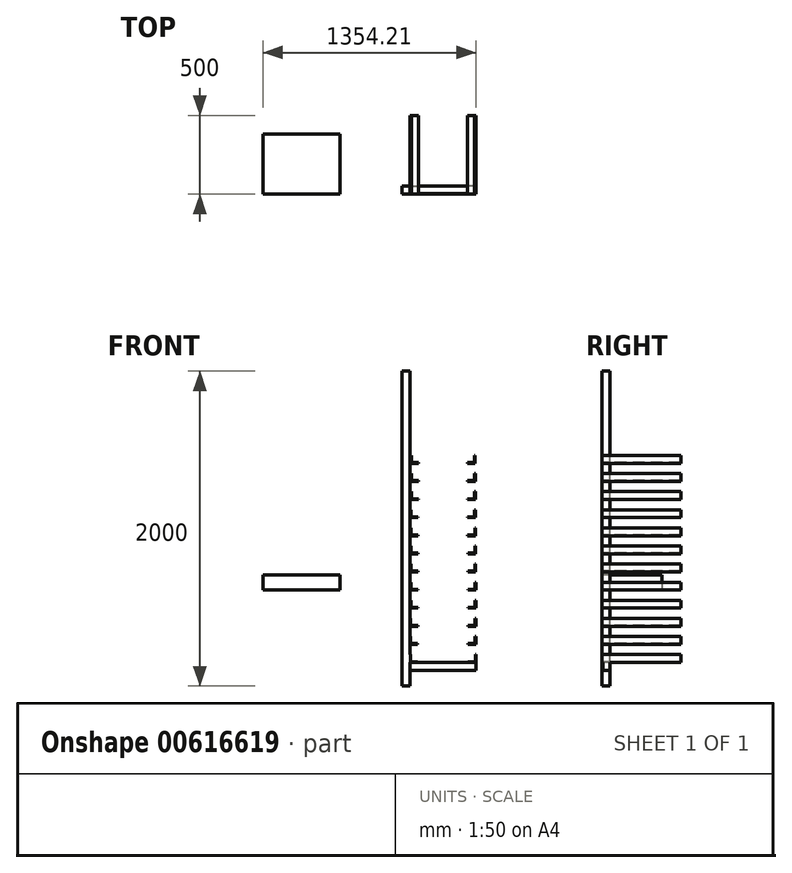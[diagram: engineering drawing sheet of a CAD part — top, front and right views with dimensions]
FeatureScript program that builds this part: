
annotation { "Feature Type Name" : "Feature", "Feature Type Description" : "" }
export const myFeature = defineFeature(function(context is Context, id is Id, definition is map)
    precondition{}
    {
        {
            var Q0;
            Q0=qCreatedBy(makeId("Front.planeOp"),FACE);
            var sketch = newSketch(context, id + "F0", { "sketchPlane" : qUnion([Q0])});
            skLineSegment(sketch, "E0.bottom", {"start": v(-1078.95, 84.72) * mm, "end": v(-1028.95, 84.72) * mm});
            skLineSegment(sketch, "E0.top", {"start": v(-1078.95, 2084.72) * mm, "end": v(-1028.95, 2084.72) * mm});
            skLineSegment(sketch, "E0.left", {"start": v(-1078.95, 84.72) * mm, "end": v(-1078.95, 2084.72) * mm});
            skLineSegment(sketch, "E0.right", {"start": v(-1028.95, 84.72) * mm, "end": v(-1028.95, 2084.72) * mm});
            skLineSegment(sketch, "E1.bottom", {"start": v(-1028.95, 234.72) * mm, "end": v(-607.88, 234.72) * mm});
            skLineSegment(sketch, "E1.top", {"start": v(-1028.95, 184.72) * mm, "end": v(-607.88, 184.72) * mm});
            skLineSegment(sketch, "E1.left", {"start": v(-1028.95, 234.72) * mm, "end": v(-1028.95, 184.72) * mm});
            skLineSegment(sketch, "E1.right", {"start": v(-607.88, 234.72) * mm, "end": v(-607.88, 184.72) * mm});
            skPoint(sketch, "E2", {"position": v(-1028.95, 209.72) * mm});
            skLineSegment(sketch, "E3", {"start": v(-1023.95, 284.72) * mm, "end": v(-1023.95, 239.72) * mm});
            skLineSegment(sketch, "E4", {"start": v(-1023.95, 239.72) * mm, "end": v(-978.95, 239.72) * mm});
            skLineSegment(sketch, "E5", {"start": v(-1023.95, 284.72) * mm, "end": v(-1028.95, 284.72) * mm});
            skLineSegment(sketch, "E6", {"start": v(-1028.95, 284.72) * mm, "end": v(-1028.95, 234.72) * mm});
            skLineSegment(sketch, "E7", {"start": v(-1028.95, 234.72) * mm, "end": v(-978.95, 234.72) * mm});
            skLineSegment(sketch, "E8", {"start": v(-978.95, 234.72) * mm, "end": v(-978.95, 239.72) * mm});
            skLineSegment(sketch, "E9.0.1.0", {"start": v(-1028.46, 399.72) * mm, "end": v(-1028.46, 349.72) * mm});
            skLineSegment(sketch, "E9.0.1.1", {"start": v(-1023.46, 354.72) * mm, "end": v(-978.46, 354.72) * mm});
            skLineSegment(sketch, "E9.0.1.2", {"start": v(-1028.46, 349.72) * mm, "end": v(-978.46, 349.72) * mm});
            skLineSegment(sketch, "E9.0.1.3", {"start": v(-1023.46, 399.72) * mm, "end": v(-1023.46, 354.72) * mm});
            skLineSegment(sketch, "E9.0.1.4", {"start": v(-978.46, 349.72) * mm, "end": v(-978.46, 354.72) * mm});
            skLineSegment(sketch, "E9.0.1.5", {"start": v(-1023.46, 399.72) * mm, "end": v(-1028.46, 399.72) * mm});
            skLineSegment(sketch, "E9.0.2.0", {"start": v(-1027.98, 514.72) * mm, "end": v(-1027.98, 464.72) * mm});
            skLineSegment(sketch, "E9.0.2.1", {"start": v(-1022.98, 469.72) * mm, "end": v(-977.98, 469.72) * mm});
            skLineSegment(sketch, "E9.0.2.2", {"start": v(-1027.98, 464.72) * mm, "end": v(-977.98, 464.72) * mm});
            skLineSegment(sketch, "E9.0.2.3", {"start": v(-1022.98, 514.72) * mm, "end": v(-1022.98, 469.72) * mm});
            skLineSegment(sketch, "E9.0.2.4", {"start": v(-977.98, 464.72) * mm, "end": v(-977.98, 469.72) * mm});
            skLineSegment(sketch, "E9.0.2.5", {"start": v(-1022.98, 514.72) * mm, "end": v(-1027.98, 514.72) * mm});
            skLineSegment(sketch, "E9.0.3.0", {"start": v(-1027.5, 629.72) * mm, "end": v(-1027.5, 579.72) * mm});
            skLineSegment(sketch, "E9.0.3.1", {"start": v(-1022.5, 584.72) * mm, "end": v(-977.5, 584.72) * mm});
            skLineSegment(sketch, "E9.0.3.2", {"start": v(-1027.5, 579.72) * mm, "end": v(-977.5, 579.72) * mm});
            skLineSegment(sketch, "E9.0.3.3", {"start": v(-1022.5, 629.72) * mm, "end": v(-1022.5, 584.72) * mm});
            skLineSegment(sketch, "E9.0.3.4", {"start": v(-977.5, 579.72) * mm, "end": v(-977.5, 584.72) * mm});
            skLineSegment(sketch, "E9.0.3.5", {"start": v(-1022.5, 629.72) * mm, "end": v(-1027.5, 629.72) * mm});
            skLineSegment(sketch, "E9.0.4.0", {"start": v(-1027.01, 744.72) * mm, "end": v(-1027.01, 694.72) * mm});
            skLineSegment(sketch, "E9.0.4.1", {"start": v(-1022.01, 699.72) * mm, "end": v(-977.01, 699.72) * mm});
            skLineSegment(sketch, "E9.0.4.2", {"start": v(-1027.01, 694.72) * mm, "end": v(-977.01, 694.72) * mm});
            skLineSegment(sketch, "E9.0.4.3", {"start": v(-1022.01, 744.72) * mm, "end": v(-1022.01, 699.72) * mm});
            skLineSegment(sketch, "E9.0.4.4", {"start": v(-977.01, 694.72) * mm, "end": v(-977.01, 699.72) * mm});
            skLineSegment(sketch, "E9.0.4.5", {"start": v(-1022.01, 744.72) * mm, "end": v(-1027.01, 744.72) * mm});
            skLineSegment(sketch, "E9.0.5.0", {"start": v(-1026.53, 859.72) * mm, "end": v(-1026.53, 809.72) * mm});
            skLineSegment(sketch, "E9.0.5.1", {"start": v(-1021.53, 814.72) * mm, "end": v(-976.53, 814.72) * mm});
            skLineSegment(sketch, "E9.0.5.2", {"start": v(-1026.53, 809.72) * mm, "end": v(-976.53, 809.72) * mm});
            skLineSegment(sketch, "E9.0.5.3", {"start": v(-1021.53, 859.72) * mm, "end": v(-1021.53, 814.72) * mm});
            skLineSegment(sketch, "E9.0.5.4", {"start": v(-976.53, 809.72) * mm, "end": v(-976.53, 814.72) * mm});
            skLineSegment(sketch, "E9.0.5.5", {"start": v(-1021.53, 859.72) * mm, "end": v(-1026.53, 859.72) * mm});
            skLineSegment(sketch, "E9.0.6.0", {"start": v(-1026.04, 974.71) * mm, "end": v(-1026.04, 924.71) * mm});
            skLineSegment(sketch, "E9.0.6.1", {"start": v(-1021.04, 929.71) * mm, "end": v(-976.04, 929.71) * mm});
            skLineSegment(sketch, "E9.0.6.2", {"start": v(-1026.04, 924.71) * mm, "end": v(-976.04, 924.71) * mm});
            skLineSegment(sketch, "E9.0.6.3", {"start": v(-1021.04, 974.71) * mm, "end": v(-1021.04, 929.71) * mm});
            skLineSegment(sketch, "E9.0.6.4", {"start": v(-976.04, 924.71) * mm, "end": v(-976.04, 929.71) * mm});
            skLineSegment(sketch, "E9.0.6.5", {"start": v(-1021.04, 974.71) * mm, "end": v(-1026.04, 974.71) * mm});
            skLineSegment(sketch, "E9.0.7.0", {"start": v(-1025.56, 1089.71) * mm, "end": v(-1025.56, 1039.71) * mm});
            skLineSegment(sketch, "E9.0.7.1", {"start": v(-1020.56, 1044.71) * mm, "end": v(-975.56, 1044.71) * mm});
            skLineSegment(sketch, "E9.0.7.2", {"start": v(-1025.56, 1039.71) * mm, "end": v(-975.56, 1039.71) * mm});
            skLineSegment(sketch, "E9.0.7.3", {"start": v(-1020.56, 1089.71) * mm, "end": v(-1020.56, 1044.71) * mm});
            skLineSegment(sketch, "E9.0.7.4", {"start": v(-975.56, 1039.71) * mm, "end": v(-975.56, 1044.71) * mm});
            skLineSegment(sketch, "E9.0.7.5", {"start": v(-1020.56, 1089.71) * mm, "end": v(-1025.56, 1089.71) * mm});
            skLineSegment(sketch, "E9.0.8.0", {"start": v(-1025.07, 1204.71) * mm, "end": v(-1025.07, 1154.71) * mm});
            skLineSegment(sketch, "E9.0.8.1", {"start": v(-1020.07, 1159.71) * mm, "end": v(-975.07, 1159.71) * mm});
            skLineSegment(sketch, "E9.0.8.2", {"start": v(-1025.07, 1154.71) * mm, "end": v(-975.07, 1154.71) * mm});
            skLineSegment(sketch, "E9.0.8.3", {"start": v(-1020.07, 1204.71) * mm, "end": v(-1020.07, 1159.71) * mm});
            skLineSegment(sketch, "E9.0.8.4", {"start": v(-975.07, 1154.71) * mm, "end": v(-975.07, 1159.71) * mm});
            skLineSegment(sketch, "E9.0.8.5", {"start": v(-1020.07, 1204.71) * mm, "end": v(-1025.07, 1204.71) * mm});
            skLineSegment(sketch, "E9.0.9.0", {"start": v(-1024.59, 1319.71) * mm, "end": v(-1024.59, 1269.71) * mm});
            skLineSegment(sketch, "E9.0.9.1", {"start": v(-1019.59, 1274.71) * mm, "end": v(-974.59, 1274.71) * mm});
            skLineSegment(sketch, "E9.0.9.2", {"start": v(-1024.59, 1269.71) * mm, "end": v(-974.59, 1269.71) * mm});
            skLineSegment(sketch, "E9.0.9.3", {"start": v(-1019.59, 1319.71) * mm, "end": v(-1019.59, 1274.71) * mm});
            skLineSegment(sketch, "E9.0.9.4", {"start": v(-974.59, 1269.71) * mm, "end": v(-974.59, 1274.71) * mm});
            skLineSegment(sketch, "E9.0.9.5", {"start": v(-1019.59, 1319.71) * mm, "end": v(-1024.59, 1319.71) * mm});
            skLineSegment(sketch, "E9.0.10.0", {"start": v(-1024.1, 1434.71) * mm, "end": v(-1024.1, 1384.71) * mm});
            skLineSegment(sketch, "E9.0.10.1", {"start": v(-1019.1, 1389.71) * mm, "end": v(-974.1, 1389.71) * mm});
            skLineSegment(sketch, "E9.0.10.2", {"start": v(-1024.1, 1384.71) * mm, "end": v(-974.1, 1384.71) * mm});
            skLineSegment(sketch, "E9.0.10.3", {"start": v(-1019.1, 1434.71) * mm, "end": v(-1019.1, 1389.71) * mm});
            skLineSegment(sketch, "E9.0.10.4", {"start": v(-974.1, 1384.71) * mm, "end": v(-974.1, 1389.71) * mm});
            skLineSegment(sketch, "E9.0.10.5", {"start": v(-1019.1, 1434.71) * mm, "end": v(-1024.1, 1434.71) * mm});
            skLineSegment(sketch, "E9.0.11.0", {"start": v(-1023.62, 1549.7) * mm, "end": v(-1023.62, 1499.7) * mm});
            skLineSegment(sketch, "E9.0.11.1", {"start": v(-1018.62, 1504.7) * mm, "end": v(-973.62, 1504.7) * mm});
            skLineSegment(sketch, "E9.0.11.2", {"start": v(-1023.62, 1499.7) * mm, "end": v(-973.62, 1499.7) * mm});
            skLineSegment(sketch, "E9.0.11.3", {"start": v(-1018.62, 1549.7) * mm, "end": v(-1018.62, 1504.7) * mm});
            skLineSegment(sketch, "E9.0.11.4", {"start": v(-973.62, 1499.7) * mm, "end": v(-973.62, 1504.7) * mm});
            skLineSegment(sketch, "E9.0.11.5", {"start": v(-1018.62, 1549.7) * mm, "end": v(-1023.62, 1549.7) * mm});
            skLineSegment(sketch, "E9.direction1", {"start": v(-1028.95, 234.72) * mm, "end": v(-950, 234.72) * mm, "construction": true});
            skLineSegment(sketch, "E9.direction2", {"start": v(-1028.95, 234.72) * mm, "end": v(-1028.46, 349.72) * mm, "construction": true});
            skLineSegment(sketch, "E10", {"start": v(-818.42, 234.72) * mm, "end": v(-818.42, 1014.16) * mm, "construction": true});
            skLineSegment(sketch, "E11.MirrorCS", {"start": v(-660.8, 924.71) * mm, "end": v(-660.8, 929.71) * mm});
            skLineSegment(sketch, "E12.MirrorCS", {"start": v(-616.27, 1089.71) * mm, "end": v(-611.27, 1089.71) * mm});
            skLineSegment(sketch, "E13.MirrorCS", {"start": v(-661.27, 1039.71) * mm, "end": v(-661.27, 1044.71) * mm});
            skLineSegment(sketch, "E14.MirrorCS", {"start": v(-616.27, 1044.71) * mm, "end": v(-661.27, 1044.71) * mm});
            skLineSegment(sketch, "E15.MirrorCS", {"start": v(-615.8, 929.71) * mm, "end": v(-660.8, 929.71) * mm});
            skLineSegment(sketch, "E16.MirrorCS", {"start": v(-617.24, 1319.71) * mm, "end": v(-612.24, 1319.71) * mm});
            skLineSegment(sketch, "E17.MirrorCS", {"start": v(-611.27, 1089.71) * mm, "end": v(-611.27, 1039.71) * mm});
            skLineSegment(sketch, "E18.MirrorCS", {"start": v(-618.21, 1504.7) * mm, "end": v(-663.21, 1504.7) * mm});
            skLineSegment(sketch, "E19.MirrorCS", {"start": v(-615.8, 974.71) * mm, "end": v(-610.8, 974.71) * mm});
            skLineSegment(sketch, "E20.MirrorCS", {"start": v(-617.24, 1319.71) * mm, "end": v(-617.24, 1274.71) * mm});
            skLineSegment(sketch, "E21.MirrorCS", {"start": v(-662.73, 1384.71) * mm, "end": v(-662.73, 1389.71) * mm});
            skLineSegment(sketch, "E22.MirrorCS", {"start": v(-611.76, 1204.71) * mm, "end": v(-611.76, 1154.71) * mm});
            skLineSegment(sketch, "E23.MirrorCS", {"start": v(-616.76, 1159.71) * mm, "end": v(-661.76, 1159.71) * mm});
            skLineSegment(sketch, "E24.MirrorCS", {"start": v(-617.73, 1434.71) * mm, "end": v(-617.73, 1389.71) * mm});
            skLineSegment(sketch, "E25.MirrorCS", {"start": v(-615.8, 974.71) * mm, "end": v(-615.8, 929.71) * mm});
            skLineSegment(sketch, "E26.MirrorCS", {"start": v(-617.24, 1274.71) * mm, "end": v(-662.24, 1274.71) * mm});
            skLineSegment(sketch, "E27.MirrorCS", {"start": v(-618.21, 1549.7) * mm, "end": v(-613.21, 1549.7) * mm});
            skLineSegment(sketch, "E28.MirrorCS", {"start": v(-612.73, 1384.71) * mm, "end": v(-662.73, 1384.71) * mm});
            skLineSegment(sketch, "E29.MirrorCS", {"start": v(-611.27, 1039.71) * mm, "end": v(-661.27, 1039.71) * mm});
            skLineSegment(sketch, "E30.MirrorCS", {"start": v(-612.73, 1434.71) * mm, "end": v(-612.73, 1384.71) * mm});
            skLineSegment(sketch, "E31.MirrorCS", {"start": v(-661.76, 1154.71) * mm, "end": v(-661.76, 1159.71) * mm});
            skLineSegment(sketch, "E32.MirrorCS", {"start": v(-616.27, 1089.71) * mm, "end": v(-616.27, 1044.71) * mm});
            skLineSegment(sketch, "E33.MirrorCS", {"start": v(-610.8, 974.71) * mm, "end": v(-610.8, 924.71) * mm});
            skLineSegment(sketch, "E34.MirrorCS", {"start": v(-616.76, 1204.71) * mm, "end": v(-611.76, 1204.71) * mm});
            skLineSegment(sketch, "E35.MirrorCS", {"start": v(-663.21, 1499.7) * mm, "end": v(-663.21, 1504.7) * mm});
            skLineSegment(sketch, "E36.MirrorCS", {"start": v(-618.21, 1549.7) * mm, "end": v(-618.21, 1504.7) * mm});
            skLineSegment(sketch, "E37.MirrorCS", {"start": v(-613.21, 1499.7) * mm, "end": v(-663.21, 1499.7) * mm});
            skLineSegment(sketch, "E38.MirrorCS", {"start": v(-617.73, 1389.71) * mm, "end": v(-662.73, 1389.71) * mm});
            skLineSegment(sketch, "E39.MirrorCS", {"start": v(-612.88, 284.72) * mm, "end": v(-607.88, 284.72) * mm});
            skLineSegment(sketch, "E40.MirrorCS", {"start": v(-662.24, 1269.71) * mm, "end": v(-662.24, 1274.71) * mm});
            skLineSegment(sketch, "E41.MirrorCS", {"start": v(-616.76, 1204.71) * mm, "end": v(-616.76, 1159.71) * mm});
            skLineSegment(sketch, "E42.MirrorCS", {"start": v(-658.37, 349.72) * mm, "end": v(-658.37, 354.72) * mm});
            skLineSegment(sketch, "E43.MirrorCS", {"start": v(-659.34, 579.72) * mm, "end": v(-659.34, 584.72) * mm});
            skLineSegment(sketch, "E44.MirrorCS", {"start": v(-660.3, 809.72) * mm, "end": v(-660.3, 814.72) * mm});
            skLineSegment(sketch, "E45.MirrorCS", {"start": v(-611.76, 1154.71) * mm, "end": v(-661.76, 1154.71) * mm});
            skLineSegment(sketch, "E46.MirrorCS", {"start": v(-613.21, 1549.7) * mm, "end": v(-613.21, 1499.7) * mm});
            skLineSegment(sketch, "E47.MirrorCS", {"start": v(-612.24, 1269.71) * mm, "end": v(-662.24, 1269.71) * mm});
            skLineSegment(sketch, "E48.MirrorCS", {"start": v(-617.73, 1434.71) * mm, "end": v(-612.73, 1434.71) * mm});
            skLineSegment(sketch, "E49.MirrorCS", {"start": v(-608.37, 349.72) * mm, "end": v(-658.37, 349.72) * mm});
            skLineSegment(sketch, "E50.MirrorCS", {"start": v(-615.3, 814.72) * mm, "end": v(-660.3, 814.72) * mm});
            skLineSegment(sketch, "E51.MirrorCS", {"start": v(-613.37, 354.72) * mm, "end": v(-658.37, 354.72) * mm});
            skLineSegment(sketch, "E52.MirrorCS", {"start": v(-612.24, 1319.71) * mm, "end": v(-612.24, 1269.71) * mm});
            skLineSegment(sketch, "E53.MirrorCS", {"start": v(-610.8, 924.71) * mm, "end": v(-660.8, 924.71) * mm});
            skLineSegment(sketch, "E54.MirrorCS", {"start": v(-607.88, 234.72) * mm, "end": v(-657.88, 234.72) * mm});
            skLineSegment(sketch, "E55.MirrorCS", {"start": v(-614.82, 744.72) * mm, "end": v(-614.82, 699.72) * mm});
            skLineSegment(sketch, "E56.MirrorCS", {"start": v(-609.34, 579.72) * mm, "end": v(-659.34, 579.72) * mm});
            skLineSegment(sketch, "E57.MirrorCS", {"start": v(-607.88, 284.72) * mm, "end": v(-607.88, 234.72) * mm});
            skLineSegment(sketch, "E58.MirrorCS", {"start": v(-612.88, 239.72) * mm, "end": v(-657.88, 239.72) * mm});
            skLineSegment(sketch, "E59.MirrorCS", {"start": v(-609.82, 694.72) * mm, "end": v(-659.82, 694.72) * mm});
            skLineSegment(sketch, "E60.MirrorCS", {"start": v(-614.34, 584.72) * mm, "end": v(-659.34, 584.72) * mm});
            skLineSegment(sketch, "E61.MirrorCS", {"start": v(-614.82, 699.72) * mm, "end": v(-659.82, 699.72) * mm});
            skLineSegment(sketch, "E62.MirrorCS", {"start": v(-658.85, 464.72) * mm, "end": v(-658.85, 469.72) * mm});
            skLineSegment(sketch, "E63.MirrorCS", {"start": v(-610.3, 809.72) * mm, "end": v(-660.3, 809.72) * mm});
            skLineSegment(sketch, "E64.MirrorCS", {"start": v(-609.82, 744.72) * mm, "end": v(-609.82, 694.72) * mm});
            skLineSegment(sketch, "E65.MirrorCS", {"start": v(-613.85, 514.72) * mm, "end": v(-608.85, 514.72) * mm});
            skLineSegment(sketch, "E66.MirrorCS", {"start": v(-614.82, 744.72) * mm, "end": v(-609.82, 744.72) * mm});
            skLineSegment(sketch, "E67.MirrorCS", {"start": v(-614.34, 629.72) * mm, "end": v(-614.34, 584.72) * mm});
            skLineSegment(sketch, "E68.MirrorCS", {"start": v(-608.85, 514.72) * mm, "end": v(-608.85, 464.72) * mm});
            skLineSegment(sketch, "E69.MirrorCS", {"start": v(-659.82, 694.72) * mm, "end": v(-659.82, 699.72) * mm});
            skLineSegment(sketch, "E70.MirrorCS", {"start": v(-613.85, 469.72) * mm, "end": v(-658.85, 469.72) * mm});
            skLineSegment(sketch, "E71.MirrorCS", {"start": v(-608.37, 399.72) * mm, "end": v(-608.37, 349.72) * mm});
            skLineSegment(sketch, "E72.MirrorCS", {"start": v(-657.88, 234.72) * mm, "end": v(-657.88, 239.72) * mm});
            skLineSegment(sketch, "E73.MirrorCS", {"start": v(-613.37, 399.72) * mm, "end": v(-608.37, 399.72) * mm});
            skLineSegment(sketch, "E74.MirrorCS", {"start": v(-612.88, 284.72) * mm, "end": v(-612.88, 239.72) * mm});
            skLineSegment(sketch, "E75.MirrorCS", {"start": v(-615.3, 859.72) * mm, "end": v(-610.3, 859.72) * mm});
            skLineSegment(sketch, "E76.MirrorCS", {"start": v(-609.34, 629.72) * mm, "end": v(-609.34, 579.72) * mm});
            skLineSegment(sketch, "E77.MirrorCS", {"start": v(-607.88, 234.72) * mm, "end": v(-686.82, 234.72) * mm, "construction": true});
            skLineSegment(sketch, "E78.MirrorCS", {"start": v(-607.88, 234.72) * mm, "end": v(-608.37, 349.72) * mm, "construction": true});
            skLineSegment(sketch, "E79.MirrorCS", {"start": v(-613.37, 399.72) * mm, "end": v(-613.37, 354.72) * mm});
            skLineSegment(sketch, "E80.MirrorCS", {"start": v(-615.3, 859.72) * mm, "end": v(-615.3, 814.72) * mm});
            skLineSegment(sketch, "E81.MirrorCS", {"start": v(-613.85, 514.72) * mm, "end": v(-613.85, 469.72) * mm});
            skLineSegment(sketch, "E82.MirrorCS", {"start": v(-614.34, 629.72) * mm, "end": v(-609.34, 629.72) * mm});
            skLineSegment(sketch, "E83.MirrorCS", {"start": v(-608.85, 464.72) * mm, "end": v(-658.85, 464.72) * mm});
            skLineSegment(sketch, "E84.MirrorCS", {"start": v(-610.3, 859.72) * mm, "end": v(-610.3, 809.72) * mm});
            skPoint(sketch, "E85", {"position": v(-818.42, 234.72) * mm});
            skLineSegment(sketch, "E86.bottom", {"start": v(-1028.95, 2084.72) * mm, "end": v(-607.88, 2084.72) * mm});
            skLineSegment(sketch, "E86.top", {"start": v(-1028.95, 2034.72) * mm, "end": v(-607.88, 2034.72) * mm});
            skLineSegment(sketch, "E86.left", {"start": v(-1028.95, 2084.72) * mm, "end": v(-1028.95, 2034.72) * mm});
            skLineSegment(sketch, "E86.right", {"start": v(-607.88, 2084.72) * mm, "end": v(-607.88, 2034.72) * mm});
            skSolve(sketch);
        }
        {
            var Q0;
            Q0=makeQuery(id+"F0.imprint","IMPRINT",FACE,{"disambiguationData":[TD([[makeQuery(id+"F0.imprint","IMPRINT",EDGE,{"derivedFrom":sQuery(id+"F0.wireOp",EDGE,"E18.MirrorCS")}),1.0]])]});
            var Q1;
            Q1=makeQuery(id+"F0.imprint","IMPRINT",FACE,{"disambiguationData":[TD([[makeQuery(id+"F0.imprint","IMPRINT",EDGE,{"derivedFrom":sQuery(id+"F0.wireOp",EDGE,"E12.MirrorCS")}),-1.0]])]});
            var Q2;
            Q2=makeQuery(id+"F0.imprint","IMPRINT",FACE,{"disambiguationData":[TD([[makeQuery(id+"F0.imprint","IMPRINT",EDGE,{"derivedFrom":sQuery(id+"F0.wireOp",EDGE,"E21.MirrorCS")}),-1.0]])]});
            var Q3;
            Q3=makeQuery(id+"F0.imprint","IMPRINT",FACE,{"disambiguationData":[TD([[makeQuery(id+"F0.imprint","IMPRINT",EDGE,{"derivedFrom":sQuery(id+"F0.wireOp",EDGE,"E16.MirrorCS")}),-1.0]])]});
            var Q4;
            Q4=makeQuery(id+"F0.imprint","IMPRINT",FACE,{"disambiguationData":[TD([[makeQuery(id+"F0.imprint","IMPRINT",EDGE,{"derivedFrom":sQuery(id+"F0.wireOp",EDGE,"E22.MirrorCS")}),-1.0]])]});
            var Q5;
            Q5=makeQuery(id+"F0.imprint","IMPRINT",FACE,{"disambiguationData":[TD([[makeQuery(id+"F0.imprint","IMPRINT",EDGE,{"derivedFrom":sQuery(id+"F0.wireOp",EDGE,"E43.MirrorCS")}),-1.0]])]});
            var Q6;
            Q6=makeQuery(id+"F0.imprint","IMPRINT",FACE,{"disambiguationData":[TD([[makeQuery(id+"F0.imprint","IMPRINT",EDGE,{"derivedFrom":sQuery(id+"F0.wireOp",EDGE,"E44.MirrorCS")}),-1.0]])]});
            var Q7;
            Q7=makeQuery(id+"F0.imprint","IMPRINT",FACE,{"disambiguationData":[TD([[makeQuery(id+"F0.imprint","IMPRINT",EDGE,{"derivedFrom":sQuery(id+"F0.wireOp",EDGE,"E55.MirrorCS")}),1.0]])]});
            var Q8;
            Q8=makeQuery(id+"F0.imprint","IMPRINT",FACE,{"disambiguationData":[TD([[makeQuery(id+"F0.imprint","IMPRINT",EDGE,{"derivedFrom":sQuery(id+"F0.wireOp",EDGE,"E62.MirrorCS")}),-1.0]])]});
            var Q9;
            Q9=makeQuery(id+"F0.imprint","IMPRINT",FACE,{"disambiguationData":[TD([[makeQuery(id+"F0.imprint","IMPRINT",EDGE,{"derivedFrom":sQuery(id+"F0.wireOp",EDGE,"E11.MirrorCS")}),-1.0]])]});
            var Q10;
            Q10=makeQuery(id+"F0.imprint","IMPRINT",FACE,{"disambiguationData":[TD([[makeQuery(id+"F0.imprint","IMPRINT",EDGE,{"derivedFrom":sQuery(id+"F0.wireOp",EDGE,"E42.MirrorCS")}),-1.0]])]});
            var Q11;
            Q11=makeQuery(id+"F0.imprint","IMPRINT",FACE,{"disambiguationData":[TD([[makeQuery(id+"F0.imprint","IMPRINT",EDGE,{"derivedFrom":sQuery(id+"F0.wireOp",EDGE,"E9.0.11.0")}),1.0]])]});
            var Q12;
            Q12=makeQuery(id+"F0.imprint","IMPRINT",FACE,{"disambiguationData":[TD([[makeQuery(id+"F0.imprint","IMPRINT",EDGE,{"derivedFrom":sQuery(id+"F0.wireOp",EDGE,"E9.0.10.0")}),1.0]])]});
            var Q13;
            Q13=makeQuery(id+"F0.imprint","IMPRINT",FACE,{"disambiguationData":[TD([[makeQuery(id+"F0.imprint","IMPRINT",EDGE,{"derivedFrom":sQuery(id+"F0.wireOp",EDGE,"E3")}),-1.0]])]});
            var Q14;
            Q14=makeQuery(id+"F0.imprint","IMPRINT",FACE,{"disambiguationData":[TD([[makeQuery(id+"F0.imprint","IMPRINT",EDGE,{"derivedFrom":sQuery(id+"F0.wireOp",EDGE,"E9.0.1.0")}),1.0]])]});
            var Q15;
            Q15=makeQuery(id+"F0.imprint","IMPRINT",FACE,{"disambiguationData":[TD([[makeQuery(id+"F0.imprint","IMPRINT",EDGE,{"derivedFrom":sQuery(id+"F0.wireOp",EDGE,"E39.MirrorCS")}),-1.0]])]});
            var Q16;
            Q16=makeQuery(id+"F0.imprint","IMPRINT",FACE,{"disambiguationData":[TD([[makeQuery(id+"F0.imprint","IMPRINT",EDGE,{"derivedFrom":sQuery(id+"F0.wireOp",EDGE,"E9.0.2.0")}),1.0]])]});
            var Q17;
            Q17=makeQuery(id+"F0.imprint","IMPRINT",FACE,{"disambiguationData":[TD([[makeQuery(id+"F0.imprint","IMPRINT",EDGE,{"derivedFrom":sQuery(id+"F0.wireOp",EDGE,"E9.0.3.0")}),1.0]])]});
            var Q18;
            Q18=makeQuery(id+"F0.imprint","IMPRINT",FACE,{"disambiguationData":[TD([[makeQuery(id+"F0.imprint","IMPRINT",EDGE,{"derivedFrom":sQuery(id+"F0.wireOp",EDGE,"E9.0.4.0")}),1.0]])]});
            var Q19;
            Q19=makeQuery(id+"F0.imprint","IMPRINT",FACE,{"disambiguationData":[TD([[makeQuery(id+"F0.imprint","IMPRINT",EDGE,{"derivedFrom":sQuery(id+"F0.wireOp",EDGE,"E9.0.5.0")}),1.0]])]});
            var Q20;
            Q20=makeQuery(id+"F0.imprint","IMPRINT",FACE,{"disambiguationData":[TD([[makeQuery(id+"F0.imprint","IMPRINT",EDGE,{"derivedFrom":sQuery(id+"F0.wireOp",EDGE,"E9.0.9.0")}),1.0]])]});
            var Q21;
            Q21=makeQuery(id+"F0.imprint","IMPRINT",FACE,{"disambiguationData":[TD([[makeQuery(id+"F0.imprint","IMPRINT",EDGE,{"derivedFrom":sQuery(id+"F0.wireOp",EDGE,"E9.0.8.0")}),1.0]])]});
            var Q22;
            Q22=makeQuery(id+"F0.imprint","IMPRINT",FACE,{"disambiguationData":[TD([[makeQuery(id+"F0.imprint","IMPRINT",EDGE,{"derivedFrom":sQuery(id+"F0.wireOp",EDGE,"E9.0.7.0")}),1.0]])]});
            var Q23;
            Q23=makeQuery(id+"F0.imprint","IMPRINT",FACE,{"disambiguationData":[TD([[makeQuery(id+"F0.imprint","IMPRINT",EDGE,{"derivedFrom":sQuery(id+"F0.wireOp",EDGE,"E9.0.6.0")}),1.0]])]});
            extrude(context, id + "F1", {"entities" : qUnion([Q0, Q1, Q2, Q3, Q4, Q5, Q6, Q7, Q8, Q9, Q10, Q11, Q12, Q13, Q14, Q15, Q16, Q17, Q18, Q19, Q20, Q21, Q22, Q23]), "oppositeDirection" : true, "depth" : 500 * mm, "offsetDistance" : 25 * mm});
        }
        {
            var Q0;
            {var subQ1=sQuery(id+"F0.wireOp",EDGE,"E0.bottom");Q0=makeQuery(id+"F0.imprint","IMPRINT",FACE,{"disambiguationData":[TD([[makeQuery(id+"F0.imprint","IMPRINT",EDGE,{"derivedFrom":subQ1}),1.0]])]});}
            var Q1;
            Q1=makeQuery(id+"F0.imprint","IMPRINT",FACE,{"disambiguationData":[TD([[makeQuery(id+"F0.imprint","IMPRINT",EDGE,{"derivedFrom":sQuery(id+"F0.wireOp",EDGE,"E1.bottom")}),-1.0]])]});
            extrude(context, id + "F2", {"entities" : qUnion([Q0, Q1]), "operationType" : NewBodyOperationType.ADD, "oppositeDirection" : true, "depth" : 50 * mm, "offsetDistance" : 25 * mm});
        }
        {
            var Q0;
            Q0=makeQuery(id+"F0.imprint","IMPRINT",FACE,{"disambiguationData":[TD([[makeQuery(id+"F0.imprint","IMPRINT",EDGE,{"derivedFrom":sQuery(id+"F0.wireOp",EDGE,"E1.bottom")}),-1.0]])]});
            extrude(context, id + "F3", {"entities" : qUnion([Q0]), "oppositeDirection" : true, "depth" : (5) * mm, "offsetDistance" : 25 * mm});
        }
        {
            var Q0;
            Q0=qCreatedBy(makeId("Front.planeOp"),FACE);
            var sketch = newSketch(context, id + "F4", { "sketchPlane" : qUnion([Q0])});
            skLineSegment(sketch, "E87.bottom", {"start": v(-1962.09, 791.4) * mm, "end": v(-1472.09, 791.4) * mm});
            skLineSegment(sketch, "E87.top", {"start": v(-1962.09, 695.4) * mm, "end": v(-1472.09, 695.4) * mm});
            skLineSegment(sketch, "E87.left", {"start": v(-1962.09, 791.4) * mm, "end": v(-1962.09, 695.4) * mm});
            skLineSegment(sketch, "E87.right", {"start": v(-1472.09, 791.4) * mm, "end": v(-1472.09, 695.4) * mm});
            skSolve(sketch);
        }
        {
            var Q0;
            Q0 = qSketchRegion(id + "F4", true);
            extrude(context, id + "F5", {"entities" : qUnion([Q0]), "oppositeDirection" : true, "depth" : 380 * mm, "offsetDistance" : 25 * mm});
        }
    });
